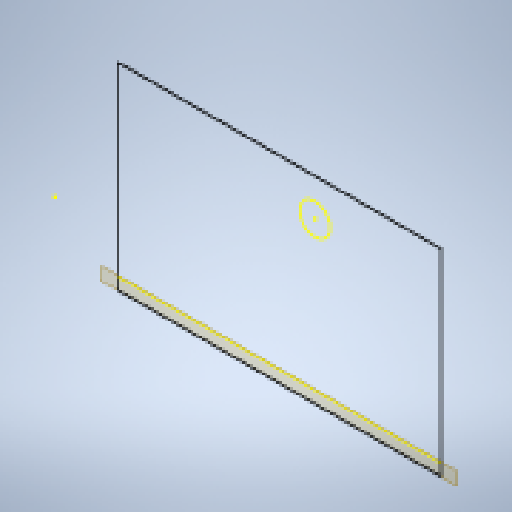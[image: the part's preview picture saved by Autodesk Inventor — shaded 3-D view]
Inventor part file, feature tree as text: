
AUTODESK INVENTOR PART (.ipt)
format: ipt  version: 2023 (Build 270158000, 158)  size: 129,024 bytes
history: native  units: mm
features: other x3, reference x2, plane x1, sketch x1
ambient origin geometry x8: Origin, YZ Plane, XZ Plane, XY Plane, X Axis, Y Axis, Z Axis, Center Point
feature tree (7):
  plane  "Work Plane1"
  sketch  "Sketch1"
  reference  "Reference1"
  reference  "Reference2"
  parser-record x1  (decoder bookkeeping rows leaked as tree rows — omitted from the tree; the rows remain in map.json)
  other  "doorLockAssembly_V4.iam"
  other  "backCase:1"
note: 1 file-system path scrubbed to <path> (originals preserved in map.json)
